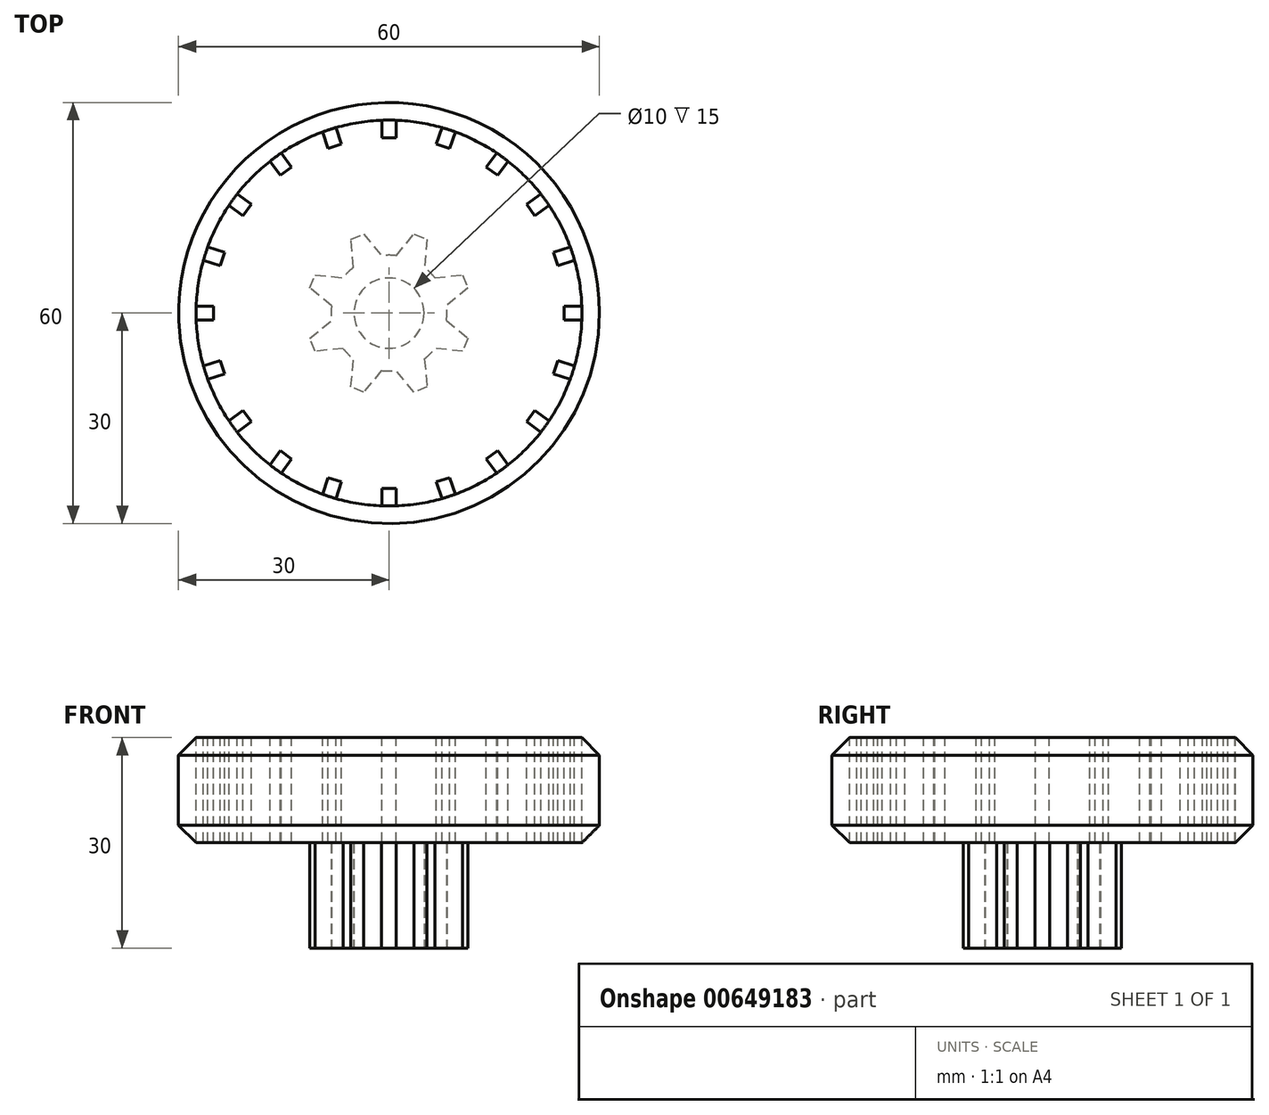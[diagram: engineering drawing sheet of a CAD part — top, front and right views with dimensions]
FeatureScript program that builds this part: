
annotation { "Feature Type Name" : "Feature", "Feature Type Description" : "" }
export const myFeature = defineFeature(function(context is Context, id is Id, definition is map)
    precondition{}
    {
        {
            var Q0;
            Q0=qCreatedBy(makeId("Top.planeOp"),FACE);
            var sketch = newSketch(context, id + "F0", { "sketchPlane" : qUnion([Q0])});
            skLineSegment(sketch, "E0", {"start": v(-8.18, 1.05) * mm, "end": v(-11.27, 3.59) * mm});
            skLineSegment(sketch, "E1", {"start": v(-11.27, 3.59) * mm, "end": v(-10.5, 5.43) * mm});
            skLineSegment(sketch, "E2", {"start": v(-10.5, 5.43) * mm, "end": v(-6.53, 5.05) * mm});
            skCircle(sketch, "E3", {"center": v(0, 0) * mm, "radius": 10 * mm, "construction": true});
            skPoint(sketch, "E4", {"position": v(-8.52, 5.24) * mm});
            skPoint(sketch, "E5", {"position": v(-9.73, 2.32) * mm});
            skArc(sketch, "E6", {"start": v(-5.05, 6.53) * mm, "mid": v(-5.83, 5.83) * mm, "end": v(-6.53, 5.05) * mm});
            skPoint(sketch, "E7", {"position": v(-11.82, 0) * mm});
            skLineSegment(sketch, "E8.1.0", {"start": v(-6.53, -5.05) * mm, "end": v(-10.5, -5.43) * mm});
            skLineSegment(sketch, "E8.1.1", {"start": v(-11.27, -3.59) * mm, "end": v(-8.18, -1.05) * mm});
            skArc(sketch, "E8.1.2", {"start": v(-8.18, 1.05) * mm, "mid": v(-8.25, 0) * mm, "end": v(-8.18, -1.05) * mm});
            skPoint(sketch, "E8.1.3", {"position": v(-9.73, -2.32) * mm});
            skPoint(sketch, "E8.1.4", {"position": v(-8.52, -5.24) * mm});
            skPoint(sketch, "E8.1.5", {"position": v(-8.36, -8.36) * mm});
            skLineSegment(sketch, "E8.1.6", {"start": v(-10.5, -5.43) * mm, "end": v(-11.27, -3.59) * mm});
            skLineSegment(sketch, "E8.2.0", {"start": v(-1.05, -8.18) * mm, "end": v(-3.59, -11.27) * mm});
            skLineSegment(sketch, "E8.2.1", {"start": v(-5.43, -10.5) * mm, "end": v(-5.05, -6.53) * mm});
            skArc(sketch, "E8.2.2", {"start": v(-6.53, -5.05) * mm, "mid": v(-5.83, -5.83) * mm, "end": v(-5.05, -6.53) * mm});
            skPoint(sketch, "E8.2.3", {"position": v(-5.24, -8.52) * mm});
            skPoint(sketch, "E8.2.4", {"position": v(-2.32, -9.73) * mm});
            skPoint(sketch, "E8.2.5", {"position": v(0, -11.82) * mm});
            skLineSegment(sketch, "E8.2.6", {"start": v(-3.59, -11.27) * mm, "end": v(-5.43, -10.5) * mm});
            skLineSegment(sketch, "E8.3.0", {"start": v(5.05, -6.53) * mm, "end": v(5.43, -10.5) * mm});
            skLineSegment(sketch, "E8.3.1", {"start": v(3.59, -11.27) * mm, "end": v(1.05, -8.18) * mm});
            skArc(sketch, "E8.3.2", {"start": v(-1.05, -8.18) * mm, "mid": v(0, -8.25) * mm, "end": v(1.05, -8.18) * mm});
            skPoint(sketch, "E8.3.3", {"position": v(2.32, -9.73) * mm});
            skPoint(sketch, "E8.3.4", {"position": v(5.24, -8.52) * mm});
            skPoint(sketch, "E8.3.5", {"position": v(8.36, -8.36) * mm});
            skLineSegment(sketch, "E8.3.6", {"start": v(5.43, -10.5) * mm, "end": v(3.59, -11.27) * mm});
            skLineSegment(sketch, "E8.4.0", {"start": v(8.18, -1.05) * mm, "end": v(11.27, -3.59) * mm});
            skLineSegment(sketch, "E8.4.1", {"start": v(10.5, -5.43) * mm, "end": v(6.53, -5.05) * mm});
            skArc(sketch, "E8.4.2", {"start": v(5.05, -6.53) * mm, "mid": v(5.83, -5.83) * mm, "end": v(6.53, -5.05) * mm});
            skPoint(sketch, "E8.4.3", {"position": v(8.52, -5.24) * mm});
            skPoint(sketch, "E8.4.4", {"position": v(9.73, -2.32) * mm});
            skPoint(sketch, "E8.4.5", {"position": v(11.82, 0) * mm});
            skLineSegment(sketch, "E8.4.6", {"start": v(11.27, -3.59) * mm, "end": v(10.5, -5.43) * mm});
            skLineSegment(sketch, "E8.5.0", {"start": v(6.53, 5.05) * mm, "end": v(10.5, 5.43) * mm});
            skLineSegment(sketch, "E8.5.1", {"start": v(11.27, 3.59) * mm, "end": v(8.18, 1.05) * mm});
            skArc(sketch, "E8.5.2", {"start": v(8.18, -1.05) * mm, "mid": v(8.25, 0) * mm, "end": v(8.18, 1.05) * mm});
            skPoint(sketch, "E8.5.3", {"position": v(9.73, 2.32) * mm});
            skPoint(sketch, "E8.5.4", {"position": v(8.52, 5.24) * mm});
            skPoint(sketch, "E8.5.5", {"position": v(8.36, 8.36) * mm});
            skLineSegment(sketch, "E8.5.6", {"start": v(10.5, 5.43) * mm, "end": v(11.27, 3.59) * mm});
            skLineSegment(sketch, "E8.6.0", {"start": v(1.05, 8.18) * mm, "end": v(3.59, 11.27) * mm});
            skLineSegment(sketch, "E8.6.1", {"start": v(5.43, 10.5) * mm, "end": v(5.05, 6.53) * mm});
            skArc(sketch, "E8.6.2", {"start": v(6.53, 5.05) * mm, "mid": v(5.83, 5.83) * mm, "end": v(5.05, 6.53) * mm});
            skPoint(sketch, "E8.6.3", {"position": v(5.24, 8.52) * mm});
            skPoint(sketch, "E8.6.4", {"position": v(2.32, 9.73) * mm});
            skPoint(sketch, "E8.6.5", {"position": v(0, 11.82) * mm});
            skLineSegment(sketch, "E8.6.6", {"start": v(3.59, 11.27) * mm, "end": v(5.43, 10.5) * mm});
            skLineSegment(sketch, "E8.7.0", {"start": v(-5.05, 6.53) * mm, "end": v(-5.43, 10.5) * mm});
            skLineSegment(sketch, "E8.7.1", {"start": v(-3.59, 11.27) * mm, "end": v(-1.05, 8.18) * mm});
            skArc(sketch, "E8.7.2", {"start": v(1.05, 8.18) * mm, "mid": v(0, 8.25) * mm, "end": v(-1.05, 8.18) * mm});
            skPoint(sketch, "E8.7.3", {"position": v(-2.32, 9.73) * mm});
            skPoint(sketch, "E8.7.4", {"position": v(-5.24, 8.52) * mm});
            skPoint(sketch, "E8.7.5", {"position": v(-8.36, 8.36) * mm});
            skLineSegment(sketch, "E8.7.6", {"start": v(-5.43, 10.5) * mm, "end": v(-3.59, 11.27) * mm});
            skCircle(sketch, "E9", {"center": v(0, 0) * mm, "radius": 5 * mm});
            skCircle(sketch, "E10", {"center": v(0, 0) * mm, "radius": 4.5 * mm});
            skPoint(sketch, "E11", {"position": v(0, 8.25) * mm});
            skSolve(sketch);
        }
        {
            var Q0;
            Q0=qSketchRegion(id+"F0",true);
            extrude(context, id + "F1", {"entities" : qUnion([Q0]), "endBound" : BoundingType.SYMMETRIC, "depth" : 15 * mm});
        }
        {
            var Q0;
            {var subQ0=sQuery(id+"F0.wireOp",EDGE,"E9");Q0=makeQuery(id+"FjRsnNbBz0NxSXN_1.boolean.opBoolean","MERGE",FACE,{"derivedFrom":[makeQuery(id+"F1.opExtrude","CAP_FACE",FACE,{"disambiguationData":[OSD([sQuery(id+"F0.wireOp",EDGE,"E0"),sQuery(id+"F0.wireOp",EDGE,"E1"),sQuery(id+"F0.wireOp",EDGE,"E2"),sQuery(id+"F0.wireOp",EDGE,"E6"),sQuery(id+"F0.wireOp",EDGE,"E8.1.0"),sQuery(id+"F0.wireOp",EDGE,"E8.1.1"),sQuery(id+"F0.wireOp",EDGE,"E8.1.2"),sQuery(id+"F0.wireOp",EDGE,"E8.1.6"),sQuery(id+"F0.wireOp",EDGE,"E8.2.0"),sQuery(id+"F0.wireOp",EDGE,"E8.2.1"),sQuery(id+"F0.wireOp",EDGE,"E8.2.2"),sQuery(id+"F0.wireOp",EDGE,"E8.2.6"),sQuery(id+"F0.wireOp",EDGE,"E8.3.0"),sQuery(id+"F0.wireOp",EDGE,"E8.3.1"),sQuery(id+"F0.wireOp",EDGE,"E8.3.2"),sQuery(id+"F0.wireOp",EDGE,"E8.3.6"),sQuery(id+"F0.wireOp",EDGE,"E8.4.0"),sQuery(id+"F0.wireOp",EDGE,"E8.4.1"),sQuery(id+"F0.wireOp",EDGE,"E8.4.2"),sQuery(id+"F0.wireOp",EDGE,"E8.4.6"),sQuery(id+"F0.wireOp",EDGE,"E8.5.0"),sQuery(id+"F0.wireOp",EDGE,"E8.5.1"),sQuery(id+"F0.wireOp",EDGE,"E8.5.2"),sQuery(id+"F0.wireOp",EDGE,"E8.5.6"),sQuery(id+"F0.wireOp",EDGE,"E8.6.0"),sQuery(id+"F0.wireOp",EDGE,"E8.6.1"),sQuery(id+"F0.wireOp",EDGE,"E8.6.2"),sQuery(id+"F0.wireOp",EDGE,"E8.6.6"),sQuery(id+"F0.wireOp",EDGE,"E8.7.0"),sQuery(id+"F0.wireOp",EDGE,"E8.7.1"),sQuery(id+"F0.wireOp",EDGE,"E8.7.2"),sQuery(id+"F0.wireOp",EDGE,"E8.7.6"),subQ0])],"isStart":false}),makeQuery(id+"FjRsnNbBz0NxSXN_1.opExtrude","CAP_FACE",FACE,{"disambiguationData":[OSD([subQ0,sQuery(id+"F0.wireOp",EDGE,"E10")])],"isStart":false})]});}
            var sketch = newSketch(context, id + "F2", { "sketchPlane" : qUnion([Q0])});
            skCircle(sketch, "E12", {"center": v(0, 0) * mm, "radius": 30 * mm});
            skSolve(sketch);
        }
        {
            var Q0;
            Q0=qSketchRegion(id+"F2",true);
            extrude(context, id + "F3", {"entities" : qUnion([Q0]), "operationType" : NewBodyOperationType.ADD, "depth" : 15 * mm});
        }
        {
            var Q0;
            Q0=makeQuery(id+"F3.opExtrude","CAP_EDGE",EDGE,{"disambiguationData":[OSD([sQuery(id+"F2.wireOp",EDGE,"E12")])],"isStart":false});
            var Q1;
            Q1=makeQuery(id+"F3.opExtrude","CAP_EDGE",EDGE,{"disambiguationData":[OSD([sQuery(id+"F2.wireOp",EDGE,"E12")])],"isStart":true});
            chamfer(context, id + "F4", {"entities" : qUnion([Q0, Q1]), "width" : 2.5 * mm, "tangentPropagation" : true});
        }
        {
            var Q0;
            Q0=makeQuery(id+"F3.opExtrude","CAP_FACE",FACE,{"disambiguationData":[OSD([sQuery(id+"F2.wireOp",EDGE,"E12")])],"isStart":false});
            var sketch = newSketch(context, id + "F5", { "sketchPlane" : qUnion([Q0])});
            skLineSegment(sketch, "E13.top", {"start": v(1, 24.98) * mm, "end": v(-1, 24.98) * mm});
            skLineSegment(sketch, "E13.left", {"start": v(1, 27.48) * mm, "end": v(1, 24.98) * mm});
            skLineSegment(sketch, "E13.right", {"start": v(-1, 27.48) * mm, "end": v(-1, 24.98) * mm});
            skPoint(sketch, "E13.middle", {"position": v(0, 26.23) * mm});
            skArc(sketch, "E14", {"start": v(1, 27.48) * mm, "mid": v(0, 27.5) * mm, "end": v(-1, 27.48) * mm});
            skLineSegment(sketch, "E15.1.0", {"start": v(-9.44, 25.83) * mm, "end": v(-8.67, 23.45) * mm});
            skPoint(sketch, "E15.1.1", {"position": v(-8.1, 24.95) * mm});
            skLineSegment(sketch, "E15.1.2", {"start": v(-7.54, 26.45) * mm, "end": v(-6.77, 24.07) * mm});
            skLineSegment(sketch, "E15.1.3", {"start": v(-6.77, 24.07) * mm, "end": v(-8.67, 23.45) * mm});
            skArc(sketch, "E15.1.4", {"start": v(-7.54, 26.45) * mm, "mid": v(-8.5, 26.15) * mm, "end": v(-9.44, 25.83) * mm});
            skLineSegment(sketch, "E15.2.0", {"start": v(-16.96, 21.65) * mm, "end": v(-15.5, 19.62) * mm});
            skPoint(sketch, "E15.2.1", {"position": v(-15.42, 21.22) * mm});
            skLineSegment(sketch, "E15.2.2", {"start": v(-15.34, 22.82) * mm, "end": v(-13.87, 20.8) * mm});
            skLineSegment(sketch, "E15.2.3", {"start": v(-13.87, 20.8) * mm, "end": v(-15.5, 19.62) * mm});
            skArc(sketch, "E15.2.4", {"start": v(-15.34, 22.82) * mm, "mid": v(-16.16, 22.25) * mm, "end": v(-16.96, 21.65) * mm});
            skLineSegment(sketch, "E15.3.0", {"start": v(-22.82, 15.34) * mm, "end": v(-20.8, 13.87) * mm});
            skPoint(sketch, "E15.3.1", {"position": v(-21.22, 15.42) * mm});
            skLineSegment(sketch, "E15.3.2", {"start": v(-21.65, 16.96) * mm, "end": v(-19.62, 15.5) * mm});
            skLineSegment(sketch, "E15.3.3", {"start": v(-19.62, 15.5) * mm, "end": v(-20.8, 13.87) * mm});
            skArc(sketch, "E15.3.4", {"start": v(-21.65, 16.96) * mm, "mid": v(-22.25, 16.16) * mm, "end": v(-22.82, 15.34) * mm});
            skLineSegment(sketch, "E15.4.0", {"start": v(-26.45, 7.54) * mm, "end": v(-24.07, 6.77) * mm});
            skPoint(sketch, "E15.4.1", {"position": v(-24.95, 8.1) * mm});
            skLineSegment(sketch, "E15.4.2", {"start": v(-25.83, 9.44) * mm, "end": v(-23.45, 8.67) * mm});
            skLineSegment(sketch, "E15.4.3", {"start": v(-23.45, 8.67) * mm, "end": v(-24.07, 6.77) * mm});
            skArc(sketch, "E15.4.4", {"start": v(-25.83, 9.44) * mm, "mid": v(-26.15, 8.5) * mm, "end": v(-26.45, 7.54) * mm});
            skLineSegment(sketch, "E15.5.0", {"start": v(-27.48, -1) * mm, "end": v(-24.98, -1) * mm});
            skPoint(sketch, "E15.5.1", {"position": v(-26.23, 0) * mm});
            skLineSegment(sketch, "E15.5.2", {"start": v(-27.48, 1) * mm, "end": v(-24.98, 1) * mm});
            skLineSegment(sketch, "E15.5.3", {"start": v(-24.98, 1) * mm, "end": v(-24.98, -1) * mm});
            skArc(sketch, "E15.5.4", {"start": v(-27.48, 1) * mm, "mid": v(-27.5, 0) * mm, "end": v(-27.48, -1) * mm});
            skLineSegment(sketch, "E15.6.0", {"start": v(-25.83, -9.44) * mm, "end": v(-23.45, -8.67) * mm});
            skPoint(sketch, "E15.6.1", {"position": v(-24.95, -8.1) * mm});
            skLineSegment(sketch, "E15.6.2", {"start": v(-26.45, -7.54) * mm, "end": v(-24.07, -6.77) * mm});
            skLineSegment(sketch, "E15.6.3", {"start": v(-24.07, -6.77) * mm, "end": v(-23.45, -8.67) * mm});
            skArc(sketch, "E15.6.4", {"start": v(-26.45, -7.54) * mm, "mid": v(-26.15, -8.5) * mm, "end": v(-25.83, -9.44) * mm});
            skLineSegment(sketch, "E15.7.0", {"start": v(-21.65, -16.96) * mm, "end": v(-19.62, -15.5) * mm});
            skPoint(sketch, "E15.7.1", {"position": v(-21.22, -15.42) * mm});
            skLineSegment(sketch, "E15.7.2", {"start": v(-22.82, -15.34) * mm, "end": v(-20.8, -13.87) * mm});
            skLineSegment(sketch, "E15.7.3", {"start": v(-20.8, -13.87) * mm, "end": v(-19.62, -15.5) * mm});
            skArc(sketch, "E15.7.4", {"start": v(-22.82, -15.34) * mm, "mid": v(-22.25, -16.16) * mm, "end": v(-21.65, -16.96) * mm});
            skLineSegment(sketch, "E15.8.0", {"start": v(-15.34, -22.82) * mm, "end": v(-13.87, -20.8) * mm});
            skPoint(sketch, "E15.8.1", {"position": v(-15.42, -21.22) * mm});
            skLineSegment(sketch, "E15.8.2", {"start": v(-16.96, -21.65) * mm, "end": v(-15.5, -19.62) * mm});
            skLineSegment(sketch, "E15.8.3", {"start": v(-15.5, -19.62) * mm, "end": v(-13.87, -20.8) * mm});
            skArc(sketch, "E15.8.4", {"start": v(-16.96, -21.65) * mm, "mid": v(-16.16, -22.25) * mm, "end": v(-15.34, -22.82) * mm});
            skLineSegment(sketch, "E15.9.0", {"start": v(-7.54, -26.45) * mm, "end": v(-6.77, -24.07) * mm});
            skPoint(sketch, "E15.9.1", {"position": v(-8.1, -24.95) * mm});
            skLineSegment(sketch, "E15.9.2", {"start": v(-9.44, -25.83) * mm, "end": v(-8.67, -23.45) * mm});
            skLineSegment(sketch, "E15.9.3", {"start": v(-8.67, -23.45) * mm, "end": v(-6.77, -24.07) * mm});
            skArc(sketch, "E15.9.4", {"start": v(-9.44, -25.83) * mm, "mid": v(-8.5, -26.15) * mm, "end": v(-7.54, -26.45) * mm});
            skLineSegment(sketch, "E15.10.0", {"start": v(1, -27.48) * mm, "end": v(1, -24.98) * mm});
            skPoint(sketch, "E15.10.1", {"position": v(0, -26.23) * mm});
            skLineSegment(sketch, "E15.10.2", {"start": v(-1, -27.48) * mm, "end": v(-1, -24.98) * mm});
            skLineSegment(sketch, "E15.10.3", {"start": v(-1, -24.98) * mm, "end": v(1, -24.98) * mm});
            skArc(sketch, "E15.10.4", {"start": v(-1, -27.48) * mm, "mid": v(0, -27.5) * mm, "end": v(1, -27.48) * mm});
            skLineSegment(sketch, "E15.11.0", {"start": v(9.44, -25.83) * mm, "end": v(8.67, -23.45) * mm});
            skPoint(sketch, "E15.11.1", {"position": v(8.1, -24.95) * mm});
            skLineSegment(sketch, "E15.11.2", {"start": v(7.54, -26.45) * mm, "end": v(6.77, -24.07) * mm});
            skLineSegment(sketch, "E15.11.3", {"start": v(6.77, -24.07) * mm, "end": v(8.67, -23.45) * mm});
            skArc(sketch, "E15.11.4", {"start": v(7.54, -26.45) * mm, "mid": v(8.5, -26.15) * mm, "end": v(9.44, -25.83) * mm});
            skLineSegment(sketch, "E15.12.0", {"start": v(16.96, -21.65) * mm, "end": v(15.5, -19.62) * mm});
            skPoint(sketch, "E15.12.1", {"position": v(15.42, -21.22) * mm});
            skLineSegment(sketch, "E15.12.2", {"start": v(15.34, -22.82) * mm, "end": v(13.87, -20.8) * mm});
            skLineSegment(sketch, "E15.12.3", {"start": v(13.87, -20.8) * mm, "end": v(15.5, -19.62) * mm});
            skArc(sketch, "E15.12.4", {"start": v(15.34, -22.82) * mm, "mid": v(16.16, -22.25) * mm, "end": v(16.96, -21.65) * mm});
            skLineSegment(sketch, "E15.13.0", {"start": v(22.82, -15.34) * mm, "end": v(20.8, -13.87) * mm});
            skPoint(sketch, "E15.13.1", {"position": v(21.22, -15.42) * mm});
            skLineSegment(sketch, "E15.13.2", {"start": v(21.65, -16.96) * mm, "end": v(19.62, -15.5) * mm});
            skLineSegment(sketch, "E15.13.3", {"start": v(19.62, -15.5) * mm, "end": v(20.8, -13.87) * mm});
            skArc(sketch, "E15.13.4", {"start": v(21.65, -16.96) * mm, "mid": v(22.25, -16.16) * mm, "end": v(22.82, -15.34) * mm});
            skLineSegment(sketch, "E15.14.0", {"start": v(26.45, -7.54) * mm, "end": v(24.07, -6.77) * mm});
            skPoint(sketch, "E15.14.1", {"position": v(24.95, -8.1) * mm});
            skLineSegment(sketch, "E15.14.2", {"start": v(25.83, -9.44) * mm, "end": v(23.45, -8.67) * mm});
            skLineSegment(sketch, "E15.14.3", {"start": v(23.45, -8.67) * mm, "end": v(24.07, -6.77) * mm});
            skArc(sketch, "E15.14.4", {"start": v(25.83, -9.44) * mm, "mid": v(26.15, -8.5) * mm, "end": v(26.45, -7.54) * mm});
            skLineSegment(sketch, "E15.15.0", {"start": v(27.48, 1) * mm, "end": v(24.98, 1) * mm});
            skPoint(sketch, "E15.15.1", {"position": v(26.23, 0) * mm});
            skLineSegment(sketch, "E15.15.2", {"start": v(27.48, -1) * mm, "end": v(24.98, -1) * mm});
            skLineSegment(sketch, "E15.15.3", {"start": v(24.98, -1) * mm, "end": v(24.98, 1) * mm});
            skArc(sketch, "E15.15.4", {"start": v(27.48, -1) * mm, "mid": v(27.5, 0) * mm, "end": v(27.48, 1) * mm});
            skLineSegment(sketch, "E15.16.0", {"start": v(25.83, 9.44) * mm, "end": v(23.45, 8.67) * mm});
            skPoint(sketch, "E15.16.1", {"position": v(24.95, 8.1) * mm});
            skLineSegment(sketch, "E15.16.2", {"start": v(26.45, 7.54) * mm, "end": v(24.07, 6.77) * mm});
            skLineSegment(sketch, "E15.16.3", {"start": v(24.07, 6.77) * mm, "end": v(23.45, 8.67) * mm});
            skArc(sketch, "E15.16.4", {"start": v(26.45, 7.54) * mm, "mid": v(26.15, 8.5) * mm, "end": v(25.83, 9.44) * mm});
            skLineSegment(sketch, "E15.17.0", {"start": v(21.65, 16.96) * mm, "end": v(19.62, 15.5) * mm});
            skPoint(sketch, "E15.17.1", {"position": v(21.22, 15.42) * mm});
            skLineSegment(sketch, "E15.17.2", {"start": v(22.82, 15.34) * mm, "end": v(20.8, 13.87) * mm});
            skLineSegment(sketch, "E15.17.3", {"start": v(20.8, 13.87) * mm, "end": v(19.62, 15.5) * mm});
            skArc(sketch, "E15.17.4", {"start": v(22.82, 15.34) * mm, "mid": v(22.25, 16.16) * mm, "end": v(21.65, 16.96) * mm});
            skLineSegment(sketch, "E15.18.0", {"start": v(15.34, 22.82) * mm, "end": v(13.87, 20.8) * mm});
            skPoint(sketch, "E15.18.1", {"position": v(15.42, 21.22) * mm});
            skLineSegment(sketch, "E15.18.2", {"start": v(16.96, 21.65) * mm, "end": v(15.5, 19.62) * mm});
            skLineSegment(sketch, "E15.18.3", {"start": v(15.5, 19.62) * mm, "end": v(13.87, 20.8) * mm});
            skArc(sketch, "E15.18.4", {"start": v(16.96, 21.65) * mm, "mid": v(16.16, 22.25) * mm, "end": v(15.34, 22.82) * mm});
            skLineSegment(sketch, "E15.19.0", {"start": v(7.54, 26.45) * mm, "end": v(6.77, 24.07) * mm});
            skPoint(sketch, "E15.19.1", {"position": v(8.1, 24.95) * mm});
            skLineSegment(sketch, "E15.19.2", {"start": v(9.44, 25.83) * mm, "end": v(8.67, 23.45) * mm});
            skLineSegment(sketch, "E15.19.3", {"start": v(8.67, 23.45) * mm, "end": v(6.77, 24.07) * mm});
            skArc(sketch, "E15.19.4", {"start": v(9.44, 25.83) * mm, "mid": v(8.5, 26.15) * mm, "end": v(7.54, 26.45) * mm});
            skSolve(sketch);
        }
        {
            var Q0;
            Q0=qSketchRegion(id+"F5",true);
            extrude(context, id + "F6", {"entities" : qUnion([Q0]), "operationType" : NewBodyOperationType.REMOVE, "oppositeDirection" : true, "depth" : 25 * mm});
        }
    });
